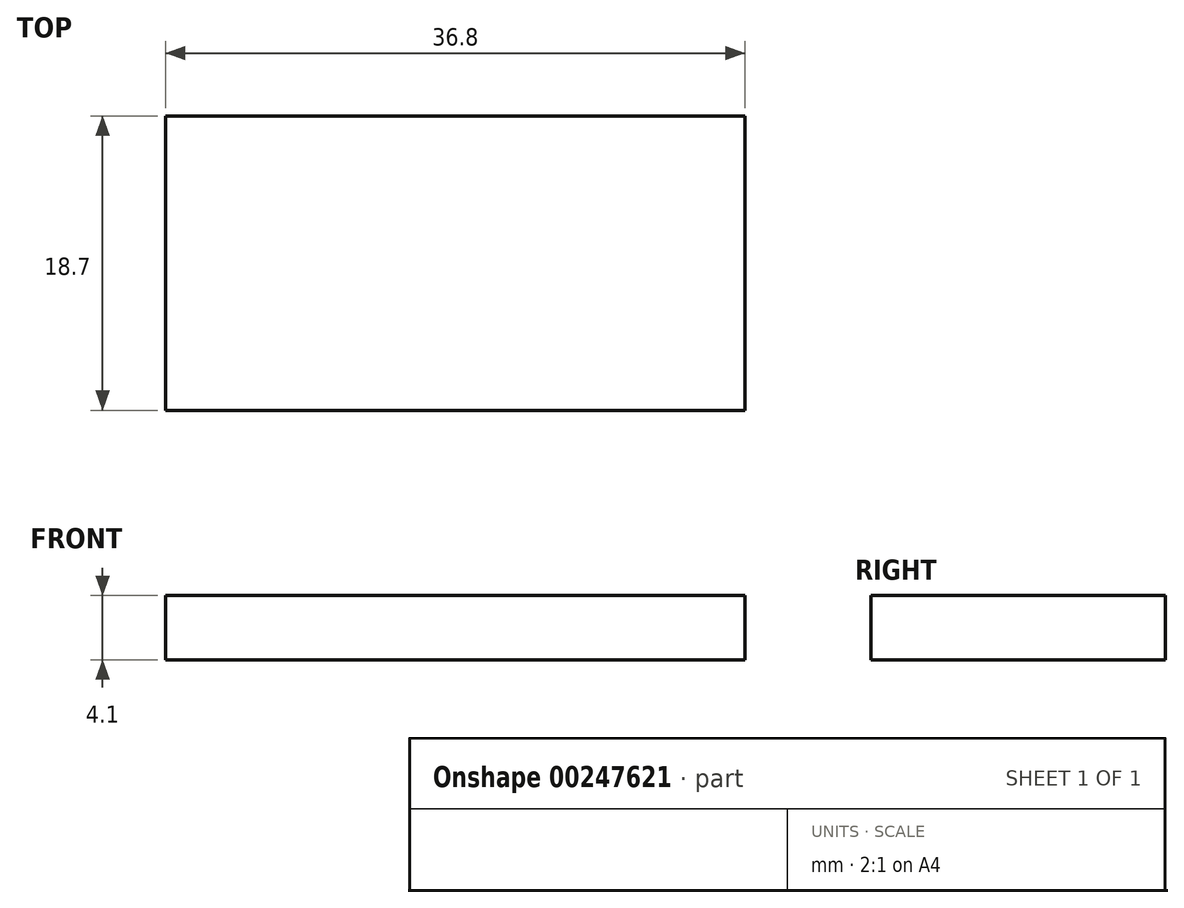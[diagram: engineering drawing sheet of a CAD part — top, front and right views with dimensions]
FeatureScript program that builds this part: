
annotation { "Feature Type Name" : "Feature", "Feature Type Description" : "" }
export const myFeature = defineFeature(function(context is Context, id is Id, definition is map)
    precondition{}
    {
        {
            var Q0;
            Q0=qCreatedBy(makeId("Top.planeOp"),FACE);
            var sketch = newSketch(context, id + "F0", { "sketchPlane" : qUnion([Q0])});
            skLineSegment(sketch, "E0.bottom", {"start": v(-18.4, 7.35) * mm, "end": v(18.4, 7.35) * mm});
            skLineSegment(sketch, "E0.top", {"start": v(-18.4, -11.35) * mm, "end": v(18.4, -11.35) * mm});
            skLineSegment(sketch, "E0.left", {"start": v(-18.4, 7.35) * mm, "end": v(-18.4, -11.35) * mm});
            skLineSegment(sketch, "E0.right", {"start": v(18.4, 7.35) * mm, "end": v(18.4, -11.35) * mm});
            skPoint(sketch, "E0.middle", {"position": v(0, -2) * mm});
            skSolve(sketch);
        }
        {
            var Q0;
            Q0 = qSketchRegion(id + "F0", true);
            extrude(context, id + "F1", {"entities" : qUnion([Q0]), "depth" : 4.1 * mm});
        }
    });
